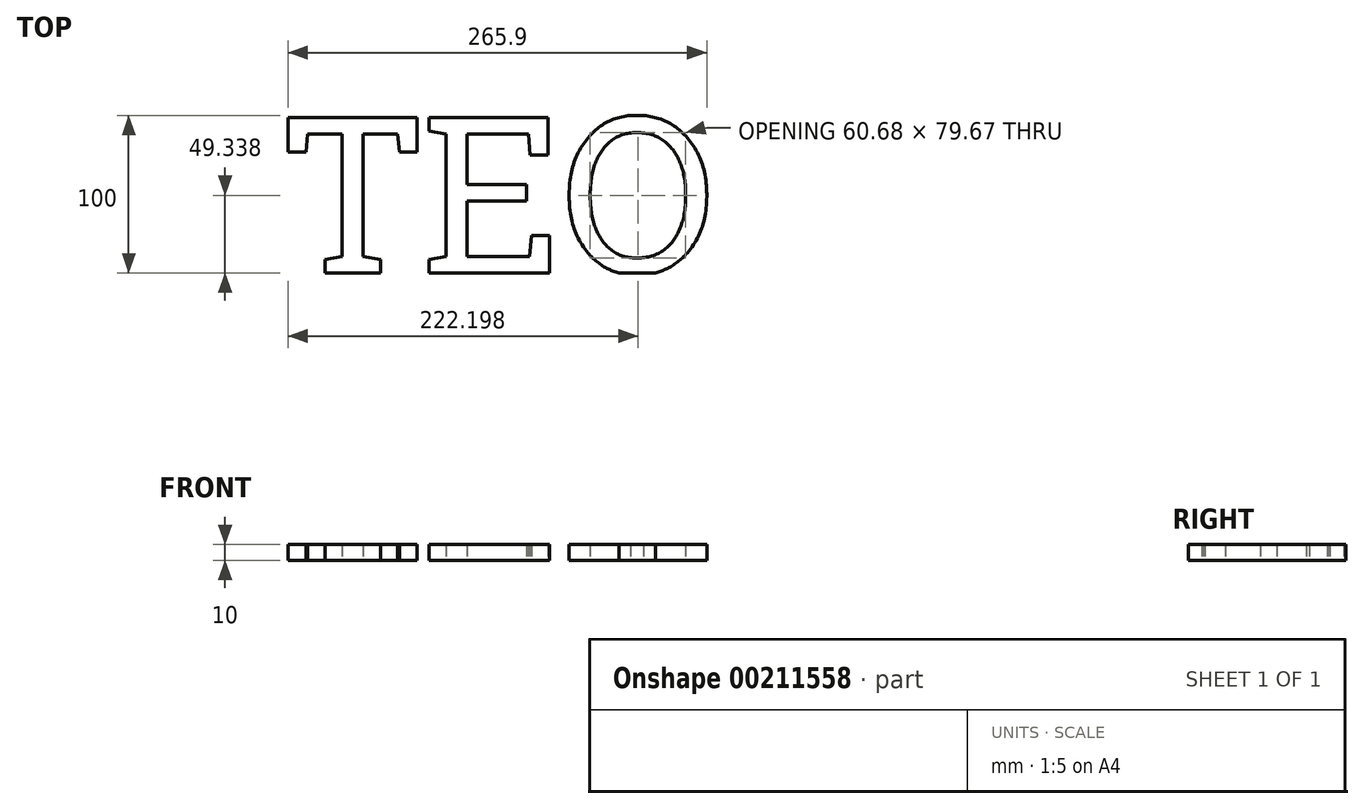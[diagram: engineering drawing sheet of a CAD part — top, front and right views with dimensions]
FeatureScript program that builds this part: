
annotation { "Feature Type Name" : "Feature", "Feature Type Description" : "" }
export const myFeature = defineFeature(function(context is Context, id is Id, definition is map)
    precondition{}
    {
        {
            var Q0;
            Q0=qCreatedBy(makeId("Top.planeOp"),FACE);
            var sketch = newSketch(context, id + "F0", { "sketchPlane" : qUnion([Q0])});
            skLineSegment(sketch, "E0.bottom", {"start": v(-138.52, 50) * mm, "end": v(138.52, 50) * mm});
            skLineSegment(sketch, "E0.top", {"start": v(-138.52, -50) * mm, "end": v(138.52, -50) * mm});
            skLineSegment(sketch, "E0.left", {"start": v(-138.52, 50) * mm, "end": v(-138.52, -50) * mm});
            skLineSegment(sketch, "E0.right", {"start": v(138.52, 50) * mm, "end": v(138.52, -50) * mm});
            skPoint(sketch, "E0.middle", {"position": v(0, 0) * mm});
            skText(sketch, "E1", { "text": "TEO", "fontName": "RobotoSlab-Regular.ttf"});
            const initialGuessF0  = {"E1": [-0.13852, -0.05, 1, 0, 0.1]};
            skSetInitialGuess(sketch, initialGuessF0);
            skSolve(sketch);
        }
        {
            var Q0;
            Q0=makeQuery(id+"F0.imprint","IMPRINT",FACE,{"disambiguationData":[TD([[makeQuery(id+"F0.imprint","IMPRINT",EDGE,{"derivedFrom":sQuery(id+"F0.wireOp",EDGE,"E1.sketch_text.stroke-0")}),-1.0]])]});
            var Q1;
            Q1=makeQuery(id+"F0.imprint","IMPRINT",FACE,{"disambiguationData":[TD([[makeQuery(id+"F0.imprint","IMPRINT",EDGE,{"derivedFrom":sQuery(id+"F0.wireOp",EDGE,"E1.sketch_text.stroke-16")}),-1.0]])]});
            var Q2;
            {var subQ5=sQuery(id+"F0.wireOp",EDGE,"E1.sketch_text.stroke-36");Q2=makeQuery(id+"F0.imprint","IMPRINT",FACE,{"disambiguationData":[TD([[makeQuery(id+"F0.imprint","IMPRINT",EDGE,{"derivedFrom":subQ5}),-1.0]])]});}
            extrude(context, id + "F1", {"entities" : qUnion([Q0, Q1, Q2]), "depth" : 10 * mm});
        }
    });
